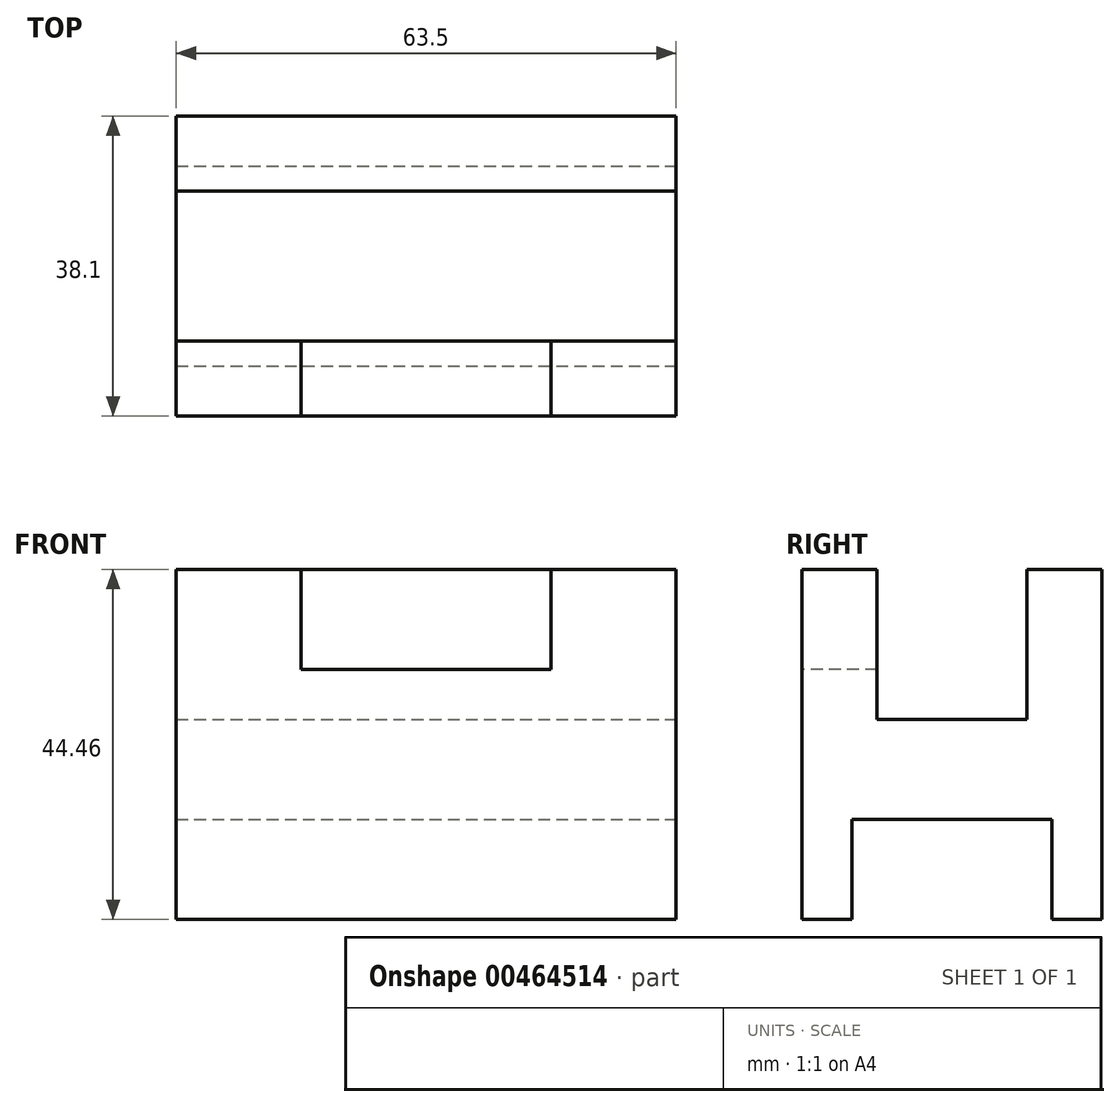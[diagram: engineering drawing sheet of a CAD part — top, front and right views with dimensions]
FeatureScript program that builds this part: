
annotation { "Feature Type Name" : "Feature", "Feature Type Description" : "" }
export const myFeature = defineFeature(function(context is Context, id is Id, definition is map)
    precondition{}
    {
        {
            var Q0;
            Q0=qCreatedBy(makeId("Front.planeOp"),FACE);
            var sketch = newSketch(context, id + "F0", { "sketchPlane" : qUnion([Q0])});
            skLineSegment(sketch, "E0.bottom", {"start": v(31.75, 22.23) * mm, "end": v(-31.75, 22.23) * mm});
            skLineSegment(sketch, "E0.top", {"start": v(31.75, -22.23) * mm, "end": v(-31.75, -22.23) * mm});
            skLineSegment(sketch, "E0.left", {"start": v(31.75, 22.23) * mm, "end": v(31.75, -22.23) * mm});
            skLineSegment(sketch, "E0.right", {"start": v(-31.75, 22.23) * mm, "end": v(-31.75, -22.23) * mm});
            skPoint(sketch, "E0.middle", {"position": v(0, 0) * mm});
            skSolve(sketch);
        }
        {
            var Q0;
            Q0=qSketchRegion(id+"F0",true);
            extrude(context, id + "F1", {"entities" : qUnion([Q0]), "depth" : 38.1 * mm});
        }
        {
            var Q0;
            Q0=makeQuery(id+"F1.opExtrude","CAP_FACE",FACE,{"disambiguationData":[OSD([sQuery(id+"F0.wireOp",EDGE,"E0.bottom"),sQuery(id+"F0.wireOp",EDGE,"E0.top"),sQuery(id+"F0.wireOp",EDGE,"E0.left"),sQuery(id+"F0.wireOp",EDGE,"E0.right")])],"isStart":false});
            var sketch = newSketch(context, id + "F2", { "sketchPlane" : qUnion([Q0])});
            skLineSegment(sketch, "E1.bottom", {"start": v(-15.88, 22.23) * mm, "end": v(15.87, 22.23) * mm});
            skLineSegment(sketch, "E1.top", {"start": v(-15.88, 9.53) * mm, "end": v(15.87, 9.53) * mm});
            skLineSegment(sketch, "E1.left", {"start": v(-15.88, 22.23) * mm, "end": v(-15.88, 9.53) * mm});
            skLineSegment(sketch, "E1.right", {"start": v(15.87, 22.23) * mm, "end": v(15.87, 9.53) * mm});
            skSolve(sketch);
        }
        {
            var Q0;
            Q0=qSketchRegion(id+"F2",true);
            extrude(context, id + "F3", {"entities" : qUnion([Q0]), "operationType" : NewBodyOperationType.REMOVE, "oppositeDirection" : true, "depth" : 38.1 * mm});
        }
        {
            var Q0;
            Q0=makeQuery(id+"F1.opExtrude","SWEPT_FACE",FACE,{"disambiguationData":[OSD([sQuery(id+"F0.wireOp",EDGE,"E0.left")])]});
            var sketch = newSketch(context, id + "F4", { "sketchPlane" : qUnion([Q0])});
            skLineSegment(sketch, "E2.bottom", {"start": v(-28.58, 22.23) * mm, "end": v(-9.53, 22.23) * mm});
            skLineSegment(sketch, "E2.top", {"start": v(-28.57, 3.18) * mm, "end": v(-9.53, 3.18) * mm});
            skLineSegment(sketch, "E2.left", {"start": v(-28.58, 22.23) * mm, "end": v(-28.58, 3.18) * mm});
            skLineSegment(sketch, "E2.right", {"start": v(-9.53, 22.23) * mm, "end": v(-9.53, 3.18) * mm});
            skSolve(sketch);
        }
        {
            var Q0;
            Q0=qSketchRegion(id+"F4",true);
            extrude(context, id + "F5", {"entities" : qUnion([Q0]), "operationType" : NewBodyOperationType.REMOVE, "oppositeDirection" : true, "depth" : 63.5 * mm});
        }
        {
            var Q0;
            Q0=makeQuery(id+"F1.opExtrude","SWEPT_FACE",FACE,{"disambiguationData":[OSD([sQuery(id+"F0.wireOp",EDGE,"E0.left")])]});
            var sketch = newSketch(context, id + "F6", { "sketchPlane" : qUnion([Q0])});
            skLineSegment(sketch, "E3.bottom", {"start": v(-31.75, -9.53) * mm, "end": v(-6.35, -9.53) * mm});
            skLineSegment(sketch, "E3.top", {"start": v(-31.75, -22.23) * mm, "end": v(-6.35, -22.23) * mm});
            skLineSegment(sketch, "E3.left", {"start": v(-31.75, -9.53) * mm, "end": v(-31.75, -22.23) * mm});
            skLineSegment(sketch, "E3.right", {"start": v(-6.35, -9.53) * mm, "end": v(-6.35, -22.23) * mm});
            skSolve(sketch);
        }
        {
            var Q0;
            Q0=qSketchRegion(id+"F6",true);
            extrude(context, id + "F7", {"entities" : qUnion([Q0]), "operationType" : NewBodyOperationType.REMOVE, "oppositeDirection" : true, "depth" : 63.5 * mm});
        }
        {
            var Q0;
            Q0=makeQuery(id+"F5.boolean.opBoolean","SPLIT",FACE,{"disambiguationData":[TD([makeQuery(id+"F5.opExtrude","SWEPT_FACE",FACE,{"disambiguationData":[OSD([sQuery(id+"F4.wireOp",EDGE,"E2.right")])]})])],"derivedFrom":makeQuery(id+"F3.boolean.opBoolean","COPY",FACE,{"derivedFrom":makeQuery(id+"F3.opExtrude","SWEPT_FACE",FACE,{"disambiguationData":[OSD([sQuery(id+"F2.wireOp",EDGE,"E1.top")])]})})});
            var sketch = newSketch(context, id + "F8", { "sketchPlane" : qUnion([Q0])});
            skLineSegment(sketch, "E4.bottom", {"start": v(-15.88, 0) * mm, "end": v(15.87, 0) * mm});
            skLineSegment(sketch, "E4.top", {"start": v(-15.88, -9.53) * mm, "end": v(15.87, -9.53) * mm});
            skLineSegment(sketch, "E4.left", {"start": v(-15.88, 0) * mm, "end": v(-15.88, -9.53) * mm});
            skLineSegment(sketch, "E4.right", {"start": v(15.87, 0) * mm, "end": v(15.87, -9.53) * mm});
            skSolve(sketch);
        }
        {
            var Q0;
            Q0=qSketchRegion(id+"F8",true);
            extrude(context, id + "F9", {"entities" : qUnion([Q0]), "operationType" : NewBodyOperationType.ADD, "depth" : 12.7 * mm});
        }
    });
